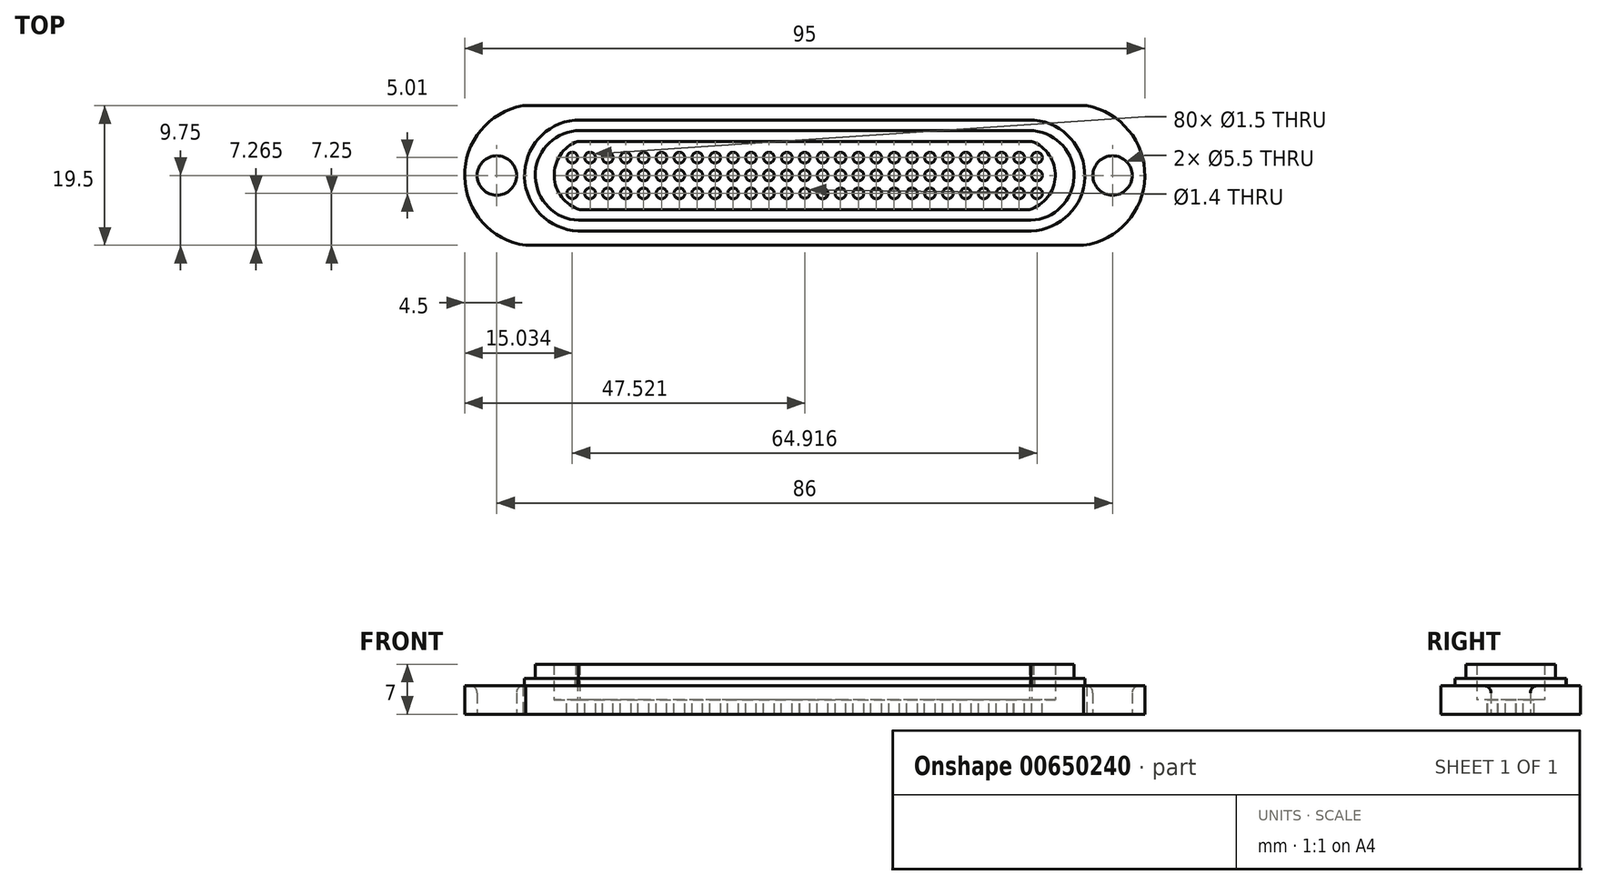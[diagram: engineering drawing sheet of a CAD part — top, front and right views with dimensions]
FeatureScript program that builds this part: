
annotation { "Feature Type Name" : "Feature", "Feature Type Description" : "" }
export const myFeature = defineFeature(function(context is Context, id is Id, definition is map)
    precondition{}
    {
        {
            var Q0;
            Q0=qCreatedBy(makeId("Top.planeOp"),FACE);
            var sketch = newSketch(context, id + "F0", { "sketchPlane" : qUnion([Q0])});
            skLineSegment(sketch, "E0.bottom", {"start": v(0, -9.75) * mm, "end": v(-38.98, -9.75) * mm});
            skLineSegment(sketch, "E0.top", {"start": v(0, 9.75) * mm, "end": v(-39.37, 9.75) * mm});
            skLineSegment(sketch, "E0.right", {"start": v(-47.5, 0) * mm, "end": v(-47.5, 0) * mm});
            skPoint(sketch, "E0.middle", {"position": v(0, 0) * mm});
            skArc(sketch, "E1", {"start": v(-39.37, 9.75) * mm, "mid": v(-47.5, -0.17) * mm, "end": v(-38.98, -9.75) * mm});
            skPoint(sketch, "E1.first.point", {"position": v(-38.98, -9.75) * mm});
            skPoint(sketch, "E1.second.point", {"position": v(-39.37, 9.75) * mm});
            skPoint(sketch, "E1.third.point", {"position": v(-47.5, 0) * mm});
            skLineSegment(sketch, "E2", {"start": v(0, 13.54) * mm, "end": v(0, -9.75) * mm, "construction": true});
            skPoint(sketch, "E3.orphan", {"position": v(-47.5, 9.75) * mm});
            skPoint(sketch, "E4.orphan", {"position": v(-47.5, -9.75) * mm});
            skPoint(sketch, "E0.left.end.orphan", {"position": v(47.5, 9.75) * mm});
            skPoint(sketch, "E0.left.start.orphan", {"position": v(47.5, -9.75) * mm});
            skLineSegment(sketch, "E5", {"start": v(-47.5, 0) * mm, "end": v(-43, 0) * mm, "construction": true});
            skCircle(sketch, "E6", {"center": v(-43, 0) * mm, "radius": 2.75 * mm});
            skLineSegment(sketch, "E7.MirrorCS", {"start": v(47.5, 0) * mm, "end": v(47.5, 0) * mm});
            skLineSegment(sketch, "E8.MirrorCS", {"start": v(47.5, 0) * mm, "end": v(43, 0) * mm, "construction": true});
            skPoint(sketch, "E9.MirrorP", {"position": v(39.37, 9.75) * mm});
            skArc(sketch, "E10.MirrorCS", {"start": v(39.37, 9.75) * mm, "mid": v(47.5, -0.17) * mm, "end": v(38.98, -9.75) * mm});
            skPoint(sketch, "E11.MirrorP", {"position": v(38.98, -9.75) * mm});
            skCircle(sketch, "E12.MirrorC", {"center": v(43, 0) * mm, "radius": 2.75 * mm});
            skPoint(sketch, "E13.MirrorP", {"position": v(47.5, 0) * mm});
            skLineSegment(sketch, "E14.MirrorCS", {"start": v(0, -9.75) * mm, "end": v(38.98, -9.75) * mm});
            skLineSegment(sketch, "E15.MirrorCS", {"start": v(0, 9.75) * mm, "end": v(39.37, 9.75) * mm});
            skLineSegment(sketch, "E16.0", {"start": v(-0.33, -6.25) * mm, "end": v(-31.59, -6.25) * mm});
            skLineSegment(sketch, "E16.2", {"start": v(-5.28, -6.25) * mm, "end": v(31.59, -6.25) * mm});
            skLineSegment(sketch, "E16.4", {"start": v(0, 6.25) * mm, "end": v(31.96, 6.25) * mm});
            skLineSegment(sketch, "E16.5", {"start": v(0, 6.25) * mm, "end": v(-31.96, 6.25) * mm});
            skLineSegment(sketch, "E17.0", {"start": v(-0.33, -4.75) * mm, "end": v(-31.39, -4.75) * mm});
            skArc(sketch, "E17.1", {"start": v(-31.71, 4.75) * mm, "mid": v(-35, -0.12) * mm, "end": v(-31.39, -4.75) * mm});
            skLineSegment(sketch, "E17.2", {"start": v(-5.28, -4.75) * mm, "end": v(31.39, -4.75) * mm});
            skArc(sketch, "E17.3", {"start": v(31.71, 4.75) * mm, "mid": v(35, -0.12) * mm, "end": v(31.39, -4.75) * mm});
            skLineSegment(sketch, "E17.4", {"start": v(0, 4.75) * mm, "end": v(31.71, 4.75) * mm});
            skLineSegment(sketch, "E17.5", {"start": v(0, 4.75) * mm, "end": v(-31.71, 4.75) * mm});
            skLineSegment(sketch, "E18", {"start": v(-0.33, -4.75) * mm, "end": v(-5.28, -4.75) * mm});
            skLineSegment(sketch, "E19", {"start": v(-5.28, -6.25) * mm, "end": v(-0.33, -6.25) * mm});
            skArc(sketch, "E20", {"start": v(-31.96, 6.25) * mm, "mid": v(-37.62, -0.17) * mm, "end": v(-31.59, -6.25) * mm});
            skArc(sketch, "E21", {"start": v(31.59, -6.25) * mm, "mid": v(37.62, -0.18) * mm, "end": v(31.96, 6.25) * mm});
            skArc(sketch, "E22.0", {"start": v(-32.1, 7.74) * mm, "mid": v(-39.12, -0.22) * mm, "end": v(-31.64, -7.75) * mm});
            skLineSegment(sketch, "E23.0", {"start": v(0, 7.75) * mm, "end": v(-31.96, 7.75) * mm});
            skLineSegment(sketch, "E24.0", {"start": v(-0.33, -7.75) * mm, "end": v(-31.59, -7.75) * mm});
            skLineSegment(sketch, "E25.MirrorCS", {"start": v(0, 7.75) * mm, "end": v(31.96, 7.75) * mm});
            skArc(sketch, "E26.MirrorCS", {"start": v(32.1, 7.74) * mm, "mid": v(39.12, -0.22) * mm, "end": v(31.64, -7.75) * mm});
            skLineSegment(sketch, "E27.MirrorCS", {"start": v(0.33, -7.75) * mm, "end": v(31.59, -7.75) * mm});
            skLineSegment(sketch, "E28", {"start": v(-0.33, -7.75) * mm, "end": v(0.33, -7.75) * mm});
            skLineSegment(sketch, "E29", {"start": v(-32.1, 7.74) * mm, "end": v(-31.96, 7.75) * mm});
            skLineSegment(sketch, "E30", {"start": v(-31.64, -7.75) * mm, "end": v(-31.59, -7.75) * mm});
            skLineSegment(sketch, "E31", {"start": v(31.59, -7.75) * mm, "end": v(31.64, -7.75) * mm});
            skLineSegment(sketch, "E32", {"start": v(31.96, 7.75) * mm, "end": v(32.1, 7.74) * mm});
            skSolve(sketch);
        }
        {
            var Q0;
            Q0=qSketchRegion(id+"F0",true);
            extrude(context, id + "F1", {"entities" : qUnion([Q0]), "depth" : 4 * mm, "offsetDistance" : 25 * mm});
        }
        {
            var Q0;
            Q0=makeQuery(id+"F0.imprint","IMPRINT",FACE,{"disambiguationData":[TD([[makeQuery(id+"F0.imprint","IMPRINT",EDGE,{"derivedFrom":sQuery(id+"F0.wireOp",EDGE,"E16.0")}),1.0]])]});
            extrude(context, id + "F2", {"entities" : qUnion([Q0]), "operationType" : NewBodyOperationType.ADD, "depth" : 5 * mm, "offsetDistance" : 25 * mm});
        }
        {
            var Q0;
            Q0=makeQuery(id+"F0.imprint","IMPRINT",FACE,{"disambiguationData":[TD([[makeQuery(id+"F0.imprint","IMPRINT",EDGE,{"derivedFrom":sQuery(id+"F0.wireOp",EDGE,"E16.0")}),-1.0]])]});
            extrude(context, id + "F3", {"entities" : qUnion([Q0]), "operationType" : NewBodyOperationType.ADD, "depth" : 7 * mm, "offsetDistance" : 25 * mm});
        }
        {
            var Q0;
            Q0=makeQuery(id+"F0.imprint","IMPRINT",FACE,{"disambiguationData":[TD([[makeQuery(id+"F0.imprint","IMPRINT",EDGE,{"derivedFrom":sQuery(id+"F0.wireOp",EDGE,"E17.0")}),-1.0]])]});
            extrude(context, id + "F4", {"entities" : qUnion([Q0]), "operationType" : NewBodyOperationType.ADD, "depth" : 2 * mm, "offsetDistance" : 25 * mm});
        }
        {
            var Q0;
            Q0=makeQuery(id+"F4.opExtrude","CAP_FACE",FACE,{"disambiguationData":[OSD([sQuery(id+"F0.wireOp",EDGE,"E17.0"),sQuery(id+"F0.wireOp",EDGE,"E17.1"),sQuery(id+"F0.wireOp",EDGE,"E17.2"),sQuery(id+"F0.wireOp",EDGE,"E17.3"),sQuery(id+"F0.wireOp",EDGE,"E17.4"),sQuery(id+"F0.wireOp",EDGE,"E17.5"),sQuery(id+"F0.wireOp",EDGE,"E18")])],"isStart":false});
            var sketch = newSketch(context, id + "F5", { "sketchPlane" : qUnion([Q0])});
            skArc(sketch, "E33", {"start": v(0, -0.75) * mm, "mid": v(0.75, 0) * mm, "end": v(0, 0.75) * mm});
            skArc(sketch, "E34.0.1.0", {"start": v(0, 1.75) * mm, "mid": v(0.75, 2.5) * mm, "end": v(0, 3.25) * mm});
            skCircle(sketch, "E34.1.0.0", {"center": v(2.5, 0) * mm, "radius": 0.75 * mm});
            skCircle(sketch, "E34.1.1.0", {"center": v(2.5, 2.5) * mm, "radius": 0.75 * mm});
            skCircle(sketch, "E34.2.0.0", {"center": v(5, 0) * mm, "radius": 0.75 * mm});
            skCircle(sketch, "E34.2.1.0", {"center": v(5, 2.5) * mm, "radius": 0.75 * mm});
            skCircle(sketch, "E34.3.0.0", {"center": v(7.5, 0) * mm, "radius": 0.75 * mm});
            skCircle(sketch, "E34.3.1.0", {"center": v(7.5, 2.5) * mm, "radius": 0.75 * mm});
            skCircle(sketch, "E34.4.0.0", {"center": v(10, 0) * mm, "radius": 0.75 * mm});
            skCircle(sketch, "E34.4.1.0", {"center": v(10, 2.5) * mm, "radius": 0.75 * mm});
            skCircle(sketch, "E34.5.0.0", {"center": v(12.5, 0) * mm, "radius": 0.75 * mm});
            skCircle(sketch, "E34.5.1.0", {"center": v(12.5, 2.5) * mm, "radius": 0.75 * mm});
            skCircle(sketch, "E34.6.0.0", {"center": v(15, 0) * mm, "radius": 0.75 * mm});
            skCircle(sketch, "E34.6.1.0", {"center": v(15, 2.5) * mm, "radius": 0.75 * mm});
            skCircle(sketch, "E34.7.0.0", {"center": v(17.5, 0) * mm, "radius": 0.75 * mm});
            skCircle(sketch, "E34.7.1.0", {"center": v(17.5, 2.5) * mm, "radius": 0.75 * mm});
            skCircle(sketch, "E34.8.0.0", {"center": v(20, 0) * mm, "radius": 0.75 * mm});
            skCircle(sketch, "E34.8.1.0", {"center": v(20, 2.5) * mm, "radius": 0.75 * mm});
            skCircle(sketch, "E34.9.0.0", {"center": v(22.5, 0) * mm, "radius": 0.75 * mm});
            skCircle(sketch, "E34.9.1.0", {"center": v(22.5, 2.5) * mm, "radius": 0.75 * mm});
            skCircle(sketch, "E34.10.0.0", {"center": v(25, 0) * mm, "radius": 0.75 * mm});
            skCircle(sketch, "E34.10.1.0", {"center": v(25, 2.5) * mm, "radius": 0.75 * mm});
            skCircle(sketch, "E34.11.0.0", {"center": v(27.5, 0) * mm, "radius": 0.75 * mm});
            skCircle(sketch, "E34.11.1.0", {"center": v(27.5, 2.5) * mm, "radius": 0.75 * mm});
            skLineSegment(sketch, "E34.direction1", {"start": v(0, 0) * mm, "end": v(2.5, 0) * mm, "construction": true});
            skLineSegment(sketch, "E34.direction2", {"start": v(0, 0) * mm, "end": v(0, 2.5) * mm, "construction": true});
            skLineSegment(sketch, "E35", {"start": v(0, 4) * mm, "end": v(0, -4) * mm, "construction": true});
            skCircle(sketch, "E36.0.1.0", {"center": v(2.5, -2.5) * mm, "radius": 0.75 * mm});
            skCircle(sketch, "E36.1.1.0", {"center": v(5, -2.5) * mm, "radius": 0.75 * mm});
            skCircle(sketch, "E36.2.1.0", {"center": v(7.5, -2.5) * mm, "radius": 0.75 * mm});
            skCircle(sketch, "E36.3.1.0", {"center": v(10, -2.5) * mm, "radius": 0.75 * mm});
            skCircle(sketch, "E36.4.1.0", {"center": v(12.5, -2.5) * mm, "radius": 0.75 * mm});
            skCircle(sketch, "E36.5.1.0", {"center": v(15, -2.5) * mm, "radius": 0.75 * mm});
            skCircle(sketch, "E36.6.1.0", {"center": v(17.5, -2.5) * mm, "radius": 0.75 * mm});
            skCircle(sketch, "E36.7.1.0", {"center": v(20, -2.5) * mm, "radius": 0.75 * mm});
            skCircle(sketch, "E36.8.1.0", {"center": v(22.5, -2.5) * mm, "radius": 0.75 * mm});
            skCircle(sketch, "E36.9.1.0", {"center": v(25, -2.5) * mm, "radius": 0.75 * mm});
            skCircle(sketch, "E36.10.1.0", {"center": v(27.5, -2.5) * mm, "radius": 0.75 * mm});
            skLineSegment(sketch, "E36.direction1", {"start": v(2.5, 0) * mm, "end": v(5, 0) * mm, "construction": true});
            skLineSegment(sketch, "E36.direction2", {"start": v(2.5, 0) * mm, "end": v(2.5, -2.5) * mm, "construction": true});
            skArc(sketch, "E37.MirrorCS", {"start": v(0, 1.75) * mm, "mid": v(-0.75, 2.5) * mm, "end": v(0, 3.25) * mm});
            skCircle(sketch, "E38.MirrorC", {"center": v(-12.5, 0) * mm, "radius": 0.75 * mm});
            skCircle(sketch, "E39.MirrorC", {"center": v(-17.5, 0) * mm, "radius": 0.75 * mm});
            skCircle(sketch, "E40.MirrorC", {"center": v(-7.5, 0) * mm, "radius": 0.75 * mm});
            skCircle(sketch, "E41.MirrorC", {"center": v(-5, 0) * mm, "radius": 0.75 * mm});
            skCircle(sketch, "E42.MirrorC", {"center": v(-15, 0) * mm, "radius": 0.75 * mm});
            skCircle(sketch, "E43.MirrorC", {"center": v(-20, 0) * mm, "radius": 0.75 * mm});
            skCircle(sketch, "E44.MirrorC", {"center": v(-10, 0) * mm, "radius": 0.75 * mm});
            skCircle(sketch, "E45.MirrorC", {"center": v(-12.5, 2.5) * mm, "radius": 0.75 * mm});
            skCircle(sketch, "E46.MirrorC", {"center": v(-10, 2.5) * mm, "radius": 0.75 * mm});
            skCircle(sketch, "E47.MirrorC", {"center": v(-7.5, 2.5) * mm, "radius": 0.75 * mm});
            skCircle(sketch, "E48.MirrorC", {"center": v(-5, 2.5) * mm, "radius": 0.75 * mm});
            skCircle(sketch, "E49.MirrorC", {"center": v(-2.5, 0) * mm, "radius": 0.75 * mm});
            skCircle(sketch, "E50.MirrorC", {"center": v(-2.5, 2.5) * mm, "radius": 0.75 * mm});
            skArc(sketch, "E51.MirrorCS", {"start": v(0, -0.75) * mm, "mid": v(-0.75, 0) * mm, "end": v(0, 0.75) * mm});
            skCircle(sketch, "E52.MirrorC", {"center": v(-17.5, 2.5) * mm, "radius": 0.75 * mm});
            skCircle(sketch, "E53.MirrorC", {"center": v(-15, 2.5) * mm, "radius": 0.75 * mm});
            skLineSegment(sketch, "E54.MirrorCS", {"start": v(0, 0) * mm, "end": v(-2.5, 0) * mm, "construction": true});
            skCircle(sketch, "E55.MirrorC", {"center": v(-20, 2.5) * mm, "radius": 0.75 * mm});
            skLineSegment(sketch, "E56.MirrorCS", {"start": v(-2.5, 0) * mm, "end": v(-2.5, -2.5) * mm, "construction": true});
            skLineSegment(sketch, "E57.MirrorCS", {"start": v(-2.5, 0) * mm, "end": v(-5, 0) * mm, "construction": true});
            skCircle(sketch, "E58.MirrorC", {"center": v(-27.5, 0) * mm, "radius": 0.75 * mm});
            skCircle(sketch, "E59.MirrorC", {"center": v(-22.5, 0) * mm, "radius": 0.75 * mm});
            skCircle(sketch, "E60.MirrorC", {"center": v(-25, 0) * mm, "radius": 0.75 * mm});
            skCircle(sketch, "E61.MirrorC", {"center": v(-27.5, -2.5) * mm, "radius": 0.75 * mm});
            skCircle(sketch, "E62.MirrorC", {"center": v(-25, 2.5) * mm, "radius": 0.75 * mm});
            skCircle(sketch, "E63.MirrorC", {"center": v(-22.5, 2.5) * mm, "radius": 0.75 * mm});
            skCircle(sketch, "E64.MirrorC", {"center": v(-17.5, -2.5) * mm, "radius": 0.75 * mm});
            skCircle(sketch, "E65.MirrorC", {"center": v(-27.5, 2.5) * mm, "radius": 0.75 * mm});
            skCircle(sketch, "E66.MirrorC", {"center": v(-20, -2.5) * mm, "radius": 0.75 * mm});
            skCircle(sketch, "E67.MirrorC", {"center": v(-22.5, -2.5) * mm, "radius": 0.75 * mm});
            skCircle(sketch, "E68.MirrorC", {"center": v(-25, -2.5) * mm, "radius": 0.75 * mm});
            skCircle(sketch, "E69.MirrorC", {"center": v(-2.5, -2.5) * mm, "radius": 0.75 * mm});
            skCircle(sketch, "E70.MirrorC", {"center": v(-5, -2.5) * mm, "radius": 0.75 * mm});
            skCircle(sketch, "E71.MirrorC", {"center": v(-7.5, -2.5) * mm, "radius": 0.75 * mm});
            skCircle(sketch, "E72.MirrorC", {"center": v(-10, -2.5) * mm, "radius": 0.75 * mm});
            skCircle(sketch, "E73.MirrorC", {"center": v(-12.5, -2.5) * mm, "radius": 0.75 * mm});
            skCircle(sketch, "E74.MirrorC", {"center": v(-15, -2.5) * mm, "radius": 0.75 * mm});
            skCircle(sketch, "E75.0.1.0", {"center": v(0.02, -2.49) * mm, "radius": 0.7 * mm});
            skLineSegment(sketch, "E76", {"start": v(-27.5, 0) * mm, "end": v(-30, 0) * mm, "construction": true});
            skCircle(sketch, "E77.MirrorC", {"center": v(-29.96, 0.04) * mm, "radius": 0.75 * mm});
            skCircle(sketch, "E78.MirrorC", {"center": v(29.96, 0.04) * mm, "radius": 0.75 * mm});
            skCircle(sketch, "E79.9.1.0", {"center": v(29.95, 2.5) * mm, "radius": 0.75 * mm});
            skCircle(sketch, "E79.10.1.0", {"center": v(32.45, 2.5) * mm, "radius": 0.75 * mm});
            skCircle(sketch, "E80.8.1.0", {"center": v(29.95, -2.5) * mm, "radius": 0.75 * mm});
            skCircle(sketch, "E80.9.0.0", {"center": v(32.45, 0) * mm, "radius": 0.75 * mm});
            skCircle(sketch, "E80.9.1.0", {"center": v(32.45, -2.5) * mm, "radius": 0.75 * mm});
            skCircle(sketch, "E81.MirrorC", {"center": v(-32.47, 0) * mm, "radius": 0.75 * mm});
            skCircle(sketch, "E82.MirrorC", {"center": v(-32.47, -2.5) * mm, "radius": 0.75 * mm});
            skCircle(sketch, "E83.MirrorC", {"center": v(-29.97, 2.5) * mm, "radius": 0.75 * mm});
            skCircle(sketch, "E84.MirrorC", {"center": v(-32.47, 2.5) * mm, "radius": 0.75 * mm});
            skCircle(sketch, "E85.MirrorC", {"center": v(-29.97, -2.5) * mm, "radius": 0.75 * mm});
            skSolve(sketch);
        }
        {
            var Q0;
            Q0=qSketchRegion(id+"F5",true);
            extrude(context, id + "F6", {"entities" : qUnion([Q0]), "operationType" : NewBodyOperationType.REMOVE, "oppositeDirection" : true, "depth" : 25 * mm, "offsetDistance" : 25 * mm});
        }
        {
            var Q0;
            Q0=makeQuery(id+"F1.opExtrude","CAP_EDGE",EDGE,{"disambiguationData":[OSD([sQuery(id+"F0.wireOp",EDGE,"E6")])],"isStart":false});
            var Q1;
            Q1=makeQuery(id+"F1.opExtrude","CAP_EDGE",EDGE,{"disambiguationData":[OSD([sQuery(id+"F0.wireOp",EDGE,"E12.MirrorC")])],"isStart":false});
            fillet(context, id + "F7", {"entities" : qUnion([Q0, Q1]), "radius" : 1 * mm, "tangentPropagation" : true, "allowEdgeOverflow" : false});
        }
    });
